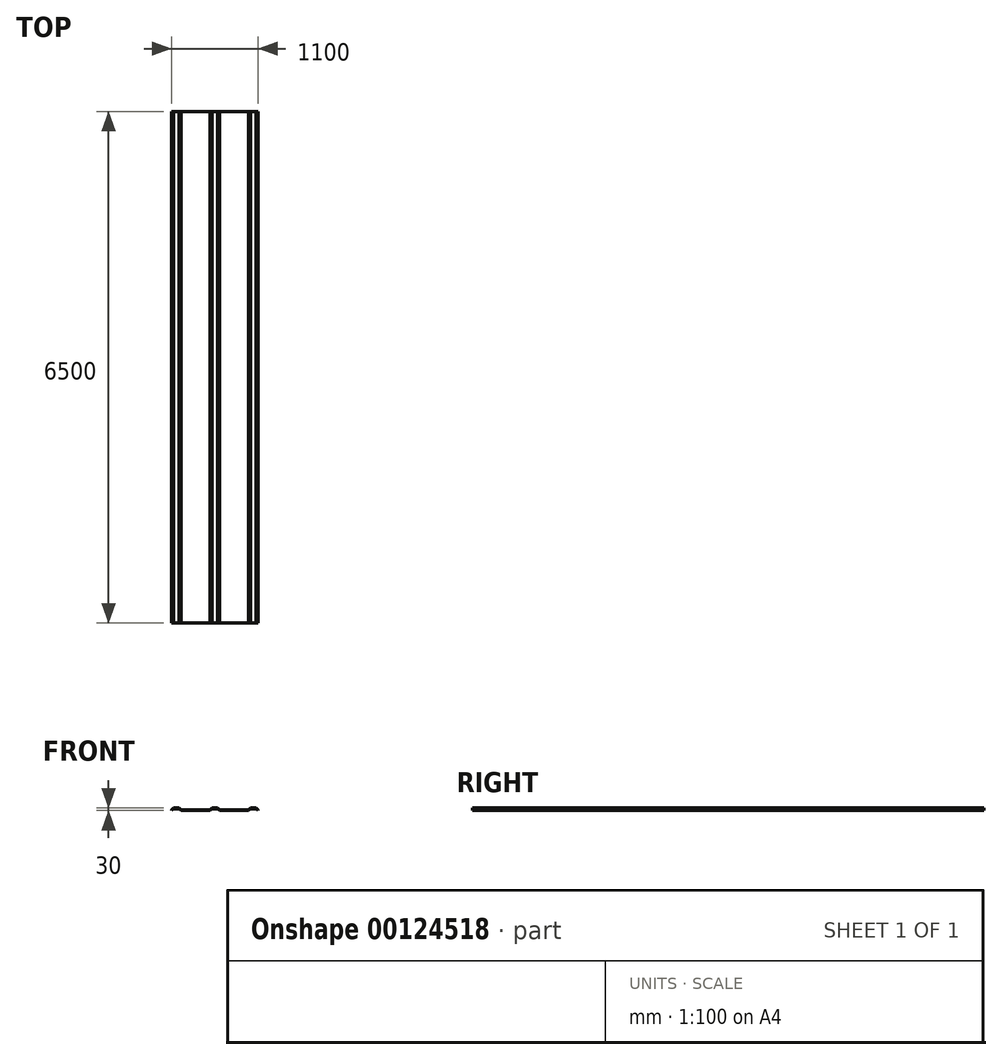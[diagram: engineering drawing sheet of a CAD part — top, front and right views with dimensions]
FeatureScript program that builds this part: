
annotation { "Feature Type Name" : "Feature", "Feature Type Description" : "" }
export const myFeature = defineFeature(function(context is Context, id is Id, definition is map)
    precondition{}
    {
        {
            var Q0;
            Q0=qCreatedBy(makeId("Front.planeOp"),FACE);
            var sketch = newSketch(context, id + "F0", { "sketchPlane" : qUnion([Q0])});
            skLineSegment(sketch, "E0", {"start": v(0, 0) * mm, "end": v(0, 0) * mm});
            skLineSegment(sketch, "E1", {"start": v(-430, 0) * mm, "end": v(-60, 0) * mm});
            skLineSegment(sketch, "E2", {"start": v(-60, 0) * mm, "end": v(-35, 20) * mm});
            skLineSegment(sketch, "E3", {"start": v(-35, 20) * mm, "end": v(35, 20) * mm});
            skLineSegment(sketch, "E4", {"start": v(35, 20) * mm, "end": v(60, 0) * mm});
            skLineSegment(sketch, "E5", {"start": v(60, 0) * mm, "end": v(430, 0) * mm});
            skLineSegment(sketch, "E6", {"start": v(430, 0) * mm, "end": v(455, 20) * mm});
            skLineSegment(sketch, "E7", {"start": v(455, 20) * mm, "end": v(525, 20) * mm});
            skLineSegment(sketch, "E8", {"start": v(525, 20) * mm, "end": v(550, 0) * mm});
            skLineSegment(sketch, "E9", {"start": v(-430, 0) * mm, "end": v(-455, 20) * mm});
            skLineSegment(sketch, "E10", {"start": v(-455, 20) * mm, "end": v(-525, 20) * mm});
            skLineSegment(sketch, "E11", {"start": v(-525, 20) * mm, "end": v(-550, 0) * mm});
            skLineSegment(sketch, "E12", {"start": v(550, 0) * mm, "end": v(550, 10) * mm});
            skLineSegment(sketch, "E13", {"start": v(550, 10) * mm, "end": v(525, 30) * mm});
            skLineSegment(sketch, "E14", {"start": v(525, 30) * mm, "end": v(455, 30) * mm});
            skLineSegment(sketch, "E15", {"start": v(455, 30) * mm, "end": v(430, 10) * mm});
            skPoint(sketch, "E15.endSnap0", {"position": v(442.5, 10) * mm});
            skLineSegment(sketch, "E16", {"start": v(430, 10) * mm, "end": v(60, 10) * mm});
            skLineSegment(sketch, "E17", {"start": v(60, 10) * mm, "end": v(35, 30) * mm});
            skLineSegment(sketch, "E18", {"start": v(35, 30) * mm, "end": v(-35, 30) * mm});
            skLineSegment(sketch, "E19", {"start": v(-35, 30) * mm, "end": v(-60, 10) * mm});
            skLineSegment(sketch, "E20", {"start": v(-60, 10) * mm, "end": v(-430, 10) * mm});
            skLineSegment(sketch, "E21", {"start": v(-430, 10) * mm, "end": v(-455, 30) * mm});
            skLineSegment(sketch, "E22", {"start": v(-455, 30) * mm, "end": v(-525, 30) * mm});
            skLineSegment(sketch, "E23", {"start": v(-525, 30) * mm, "end": v(-550, 10) * mm});
            skLineSegment(sketch, "E24", {"start": v(-550, 10) * mm, "end": v(-550, 0) * mm});
            skSolve(sketch);
        }
        {
            var Q0;
            Q0 = qSketchRegion(id + "F0", true);
            extrude(context, id + "F1", {"entities" : qUnion([Q0]), "endBound" : BoundingType.SYMMETRIC, "depth" : 6500 * mm});
        }
    });
